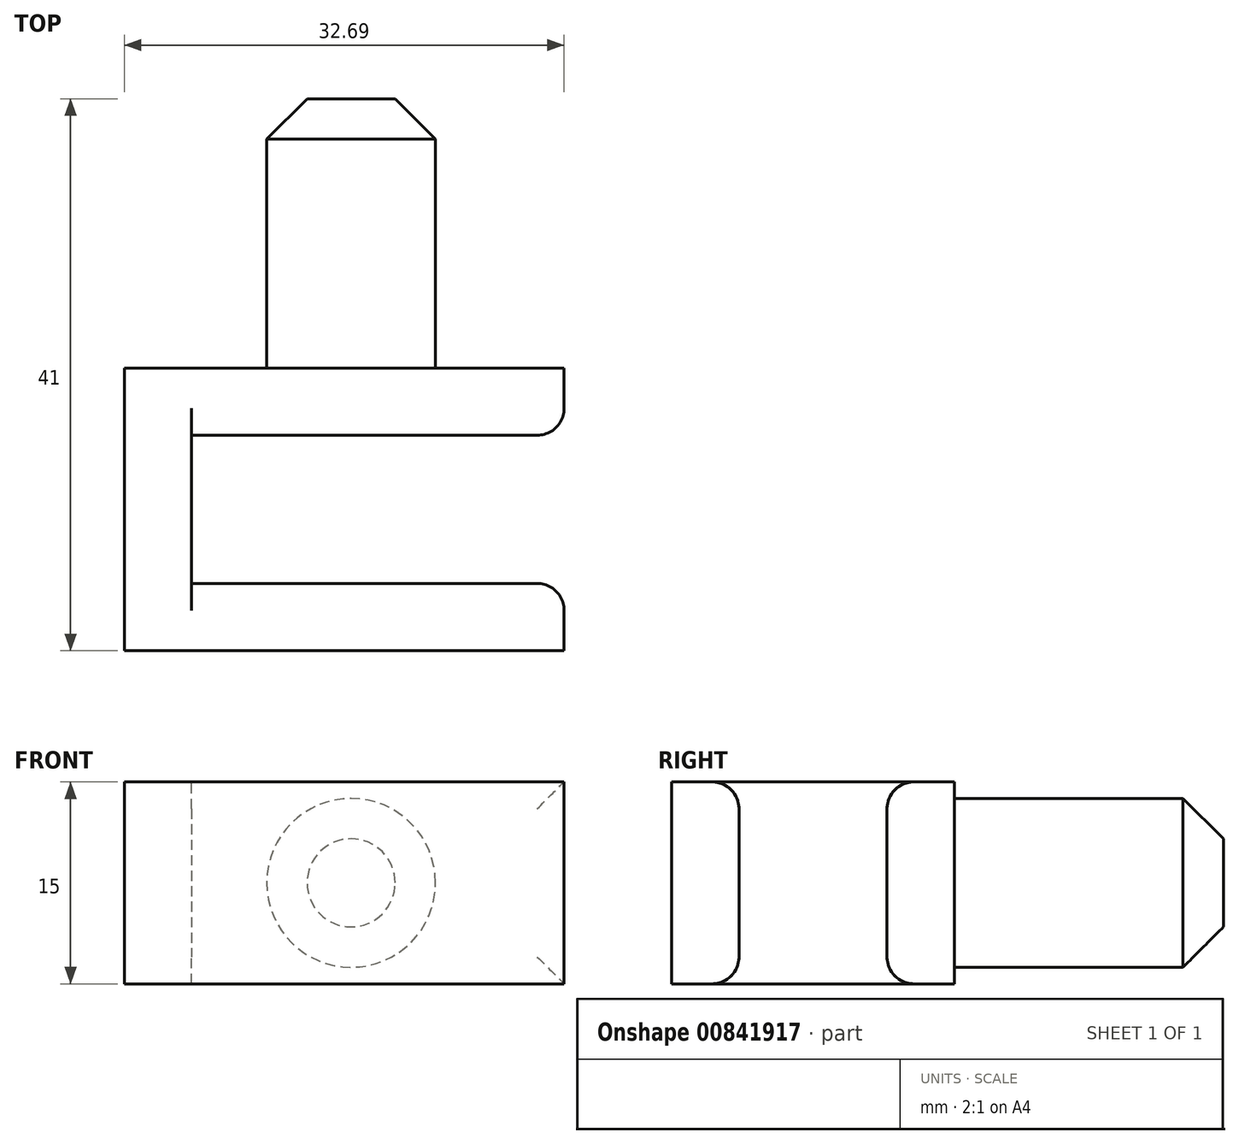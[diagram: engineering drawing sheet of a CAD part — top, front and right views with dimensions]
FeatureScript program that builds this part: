
annotation { "Feature Type Name" : "Feature", "Feature Type Description" : "" }
export const myFeature = defineFeature(function(context is Context, id is Id, definition is map)
    precondition{}
    {
        {
            var Q0;
            Q0=qCreatedBy(makeId("Top.planeOp"),FACE);
            var sketch = newSketch(context, id + "F0", { "sketchPlane" : qUnion([Q0])});
            skLineSegment(sketch, "E0", {"start": v(15.83, 0) * mm, "end": v(-16.86, 0) * mm});
            skLineSegment(sketch, "E1", {"start": v(-16.86, 0) * mm, "end": v(-16.86, -21) * mm});
            skLineSegment(sketch, "E2", {"start": v(-16.86, -21) * mm, "end": v(15.83, -21) * mm});
            skLineSegment(sketch, "E3", {"start": v(15.83, -21) * mm, "end": v(15.83, -16) * mm});
            skLineSegment(sketch, "E4", {"start": v(15.83, -16) * mm, "end": v(-11.86, -16) * mm});
            skLineSegment(sketch, "E5", {"start": v(-11.86, -16) * mm, "end": v(-11.86, -5) * mm});
            skLineSegment(sketch, "E6", {"start": v(-11.86, -5) * mm, "end": v(15.83, -5) * mm});
            skLineSegment(sketch, "E7", {"start": v(15.83, -5) * mm, "end": v(15.83, 0) * mm});
            skSolve(sketch);
        }
        {
            var Q0;
            Q0 = qSketchRegion(id + "F0", true);
            extrude(context, id + "F1", {"entities" : qUnion([Q0]), "endBound" : BoundingType.SYMMETRIC, "depth" : 15 * mm, "offsetDistance" : 25 * mm});
        }
        {
            var Q0;
            Q0=qCreatedBy(makeId("Front.planeOp"),FACE);
            var sketch = newSketch(context, id + "F2", { "sketchPlane" : qUnion([Q0])});
            skCircle(sketch, "E8", {"center": v(0, 0) * mm, "radius": 6.27 * mm});
            skSolve(sketch);
        }
        {
            var Q0;
            Q0 = qSketchRegion(id + "F2", true);
            extrude(context, id + "F3", {"entities" : qUnion([Q0]), "operationType" : NewBodyOperationType.ADD, "oppositeDirection" : true, "depth" : 20 * mm, "offsetDistance" : 25 * mm});
        }
        {
            var Q0;
            Q0=makeQuery(id+"F3.opExtrude","CAP_EDGE",EDGE,{"disambiguationData":[OSD([sQuery(id+"F2.wireOp",EDGE,"E8")])],"isStart":false});
            chamfer(context, id + "F4", {"entities" : qUnion([Q0]), "width" : 3 * mm, "tangentPropagation" : true});
        }
        {
            var Q0;
            Q0=makeQuery(id+"F1.opExtrude","CAP_EDGE",EDGE,{"disambiguationData":[OSD([sQuery(id+"F0.wireOp",EDGE,"E6")])],"isStart":true});
            var Q1;
            Q1=makeQuery(id+"F1.opExtrude","CAP_EDGE",EDGE,{"disambiguationData":[OSD([sQuery(id+"F0.wireOp",EDGE,"E4")])],"isStart":true});
            var Q2;
            Q2=makeQuery(id+"F1.opExtrude","SWEPT_EDGE",EDGE,{"disambiguationData":[OSD([sQuery(id+"F0.wireOp",EDGE,"E3"),sQuery(id+"F0.wireOp",EDGE,"E4")])]});
            var Q3;
            Q3=makeQuery(id+"F1.opExtrude","SWEPT_EDGE",EDGE,{"disambiguationData":[OSD([sQuery(id+"F0.wireOp",EDGE,"E6"),sQuery(id+"F0.wireOp",EDGE,"E7")])]});
            var Q4;
            Q4=makeQuery(id+"F1.opExtrude","CAP_EDGE",EDGE,{"disambiguationData":[OSD([sQuery(id+"F0.wireOp",EDGE,"E6")])],"isStart":false});
            var Q5;
            Q5=makeQuery(id+"F1.opExtrude","CAP_EDGE",EDGE,{"disambiguationData":[OSD([sQuery(id+"F0.wireOp",EDGE,"E4")])],"isStart":false});
            fillet(context, id + "F5", {"entities" : qUnion([Q0, Q1, Q2, Q3, Q4, Q5]), "radius" : 2 * mm, "tangentPropagation" : true, "allowEdgeOverflow" : false});
        }
    });
